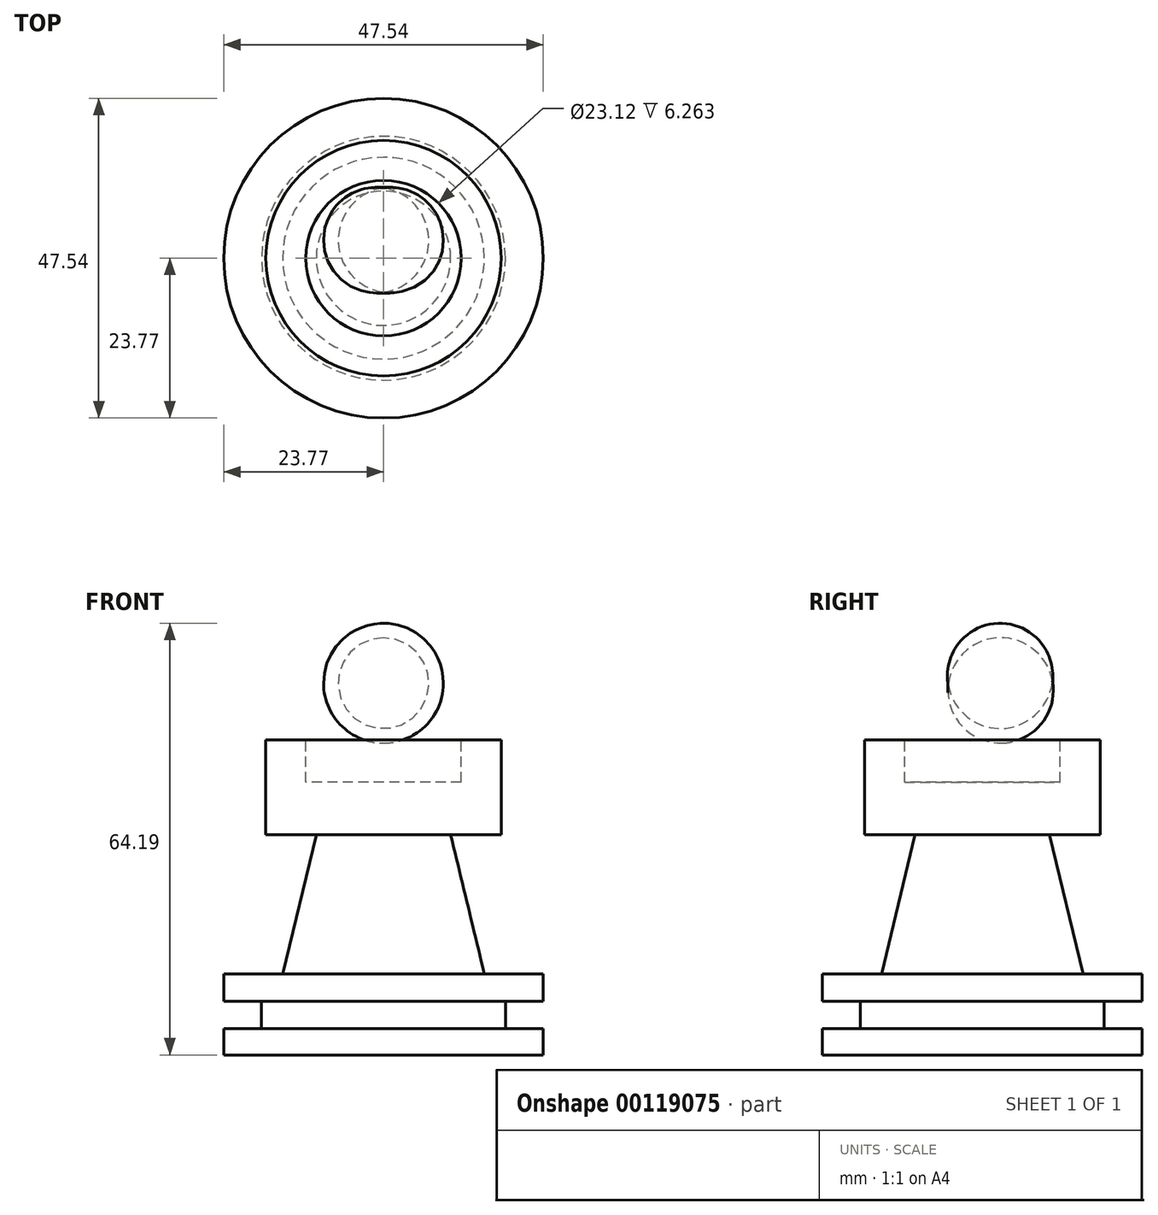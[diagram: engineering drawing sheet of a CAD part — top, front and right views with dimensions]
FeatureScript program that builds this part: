
annotation { "Feature Type Name" : "Feature", "Feature Type Description" : "" }
export const myFeature = defineFeature(function(context is Context, id is Id, definition is map)
    precondition{}
    {
        {
            var Q0;
            Q0=qCreatedBy(makeId("Front.planeOp"),FACE);
            var sketch = newSketch(context, id + "F0", { "sketchPlane" : qUnion([Q0])});
            skLineSegment(sketch, "E0", {"start": v(0, 36.17) * mm, "end": v(0, 0) * mm});
            skLineSegment(sketch, "E1", {"start": v(0, 0) * mm, "end": v(23.77, 0) * mm});
            skLineSegment(sketch, "E2", {"start": v(23.77, 0) * mm, "end": v(23.77, 3.91) * mm});
            skLineSegment(sketch, "E3", {"start": v(23.77, 3.91) * mm, "end": v(18.14, 3.91) * mm});
            skLineSegment(sketch, "E4", {"start": v(18.14, 3.91) * mm, "end": v(18.14, 7.99) * mm});
            skLineSegment(sketch, "E5", {"start": v(18.14, 7.99) * mm, "end": v(23.77, 7.99) * mm});
            skLineSegment(sketch, "E6", {"start": v(23.77, 7.99) * mm, "end": v(23.77, 12.06) * mm});
            skLineSegment(sketch, "E7", {"start": v(23.77, 12.06) * mm, "end": v(15, 12.06) * mm});
            skLineSegment(sketch, "E8", {"start": v(15, 12.06) * mm, "end": v(10, 32.72) * mm});
            skLineSegment(sketch, "E9", {"start": v(10, 32.72) * mm, "end": v(17.5, 32.72) * mm});
            skLineSegment(sketch, "E10", {"start": v(17.5, 32.72) * mm, "end": v(17.5, 46.82) * mm});
            skLineSegment(sketch, "E11", {"start": v(17.5, 46.82) * mm, "end": v(11.56, 46.82) * mm});
            skLineSegment(sketch, "E12", {"start": v(11.56, 46.82) * mm, "end": v(11.56, 40.55) * mm});
            skLineSegment(sketch, "E13", {"start": v(11.56, 40.55) * mm, "end": v(0, 40.55) * mm});
            skLineSegment(sketch, "E14", {"start": v(0, 40.55) * mm, "end": v(0, 36.17) * mm});
            skSolve(sketch);
        }
        {
            var Q0;
            Q0=makeQuery(id+"F0.imprint","IMPRINT",FACE,{"disambiguationData":[TD([[makeQuery(id+"F0.imprint","IMPRINT",EDGE,{"derivedFrom":sQuery(id+"F0.wireOp",EDGE,"E0")}),1.0]])]});
            var Q1;
            Q1=sQuery(id+"F0.wireOp",EDGE,"E0");
            revolve(context, id + "F1", {"entities" : qUnion([Q0]), "axis" : qUnion([Q1]), "revolveType" : RevolveType.FULL});
        }
        {
            var Q0;
            Q0=qCreatedBy(makeId("Right.planeOp"),FACE);
            var sketch = newSketch(context, id + "F2", { "sketchPlane" : qUnion([Q0])});
            skArc(sketch, "E15", {"start": v(10.43, 55.57) * mm, "mid": v(2.34, 64.18) * mm, "end": v(-5.07, 54.98) * mm});
            skLineSegment(sketch, "E16", {"start": v(-5.07, 54.98) * mm, "end": v(10.43, 55.57) * mm});
            skSolve(sketch);
        }
        {
            var Q0;
            Q0=makeQuery(id+"F2.imprint","IMPRINT",FACE,{"disambiguationData":[TD([[makeQuery(id+"F2.imprint","IMPRINT",EDGE,{"derivedFrom":sQuery(id+"F2.wireOp",EDGE,"E15")}),1.0]])]});
            var Q1;
            Q1=sQuery(id+"F2.wireOp",EDGE,"E16");
            revolve(context, id + "F3", {"entities" : qUnion([Q0]), "axis" : qUnion([Q1]), "revolveType" : RevolveType.FULL});
        }
    });
